# Revit family: Haworth_ActiveComponents_RectangleFullConferenceEnd_BUILD
name_source: partatom
category: Furniture Systems
revit_build: Autodesk Revit 2018 (Build: 20170223_1515(x64)
units: mm (PartAtom-declared; Revit-internal decimal feet)

## family parameters
Always vertical = Yes
Cut with Voids When Loaded = No
OmniClass Number = 23.40.70.14.64.21
OmniClass Title = Systems Furniture
Part Type = Normal
Room Calculation Point = No
Round Connector Dimension = Use Diameter
Shared = No
Work Plane-Based = No

## types (5) — shared parameters
Actual Height = 29 3/16"
Angle Leg Offset = 5 3/4"
Assembly Code = E2020200
Description = Haworth - Active Components - Rectangle Full Conference End
Manufacturer = Haworth
Max. Width = 72"
Min. Width = 60"
Model = WAYA
Radius = 4 1/2"
Revision Number = 1
Size = Verify Final Dim. w/ Haworth
Thickness = 1 3/16"
URL = www.haworth.com
URL - Product = https://www.haworth.com
Warranty = https://www.haworth.com
With Leg = Yes

## per-type parameters (varying)
| type | Actual Depth | Actual Width | Angled Leg Control | Column Leg Control | Column Leg Offset | Overall Depth | Overhang | Panel Width |
| 30d 72w - 48 Panel Width | 30" | 72" | No | Yes | 8 15/16" | 33" | 24" | 48" |
| 30d 72w - 66 Panel Width | 30" | 72" | Yes | No | 8 15/16" | 33" | 6" | 66" |
| 30d 60w - 54 Panel Width | 30" | 60" | Yes | No | 7 15/16" | 33" | 6" | 54" |
| 30d 60w - 42 Panel Width | 30" | 60" | No | Yes | 7 15/16" | 33" | 18" | 42" |
| 24d 60w - 48 Panel Width | 24" | 60" | No | Yes | 7 15/16" | 27" | 12" | 48" |

## geometry (parser evidence)
native form markers: Sweep x9
no freeform markers — native parametric forms only
